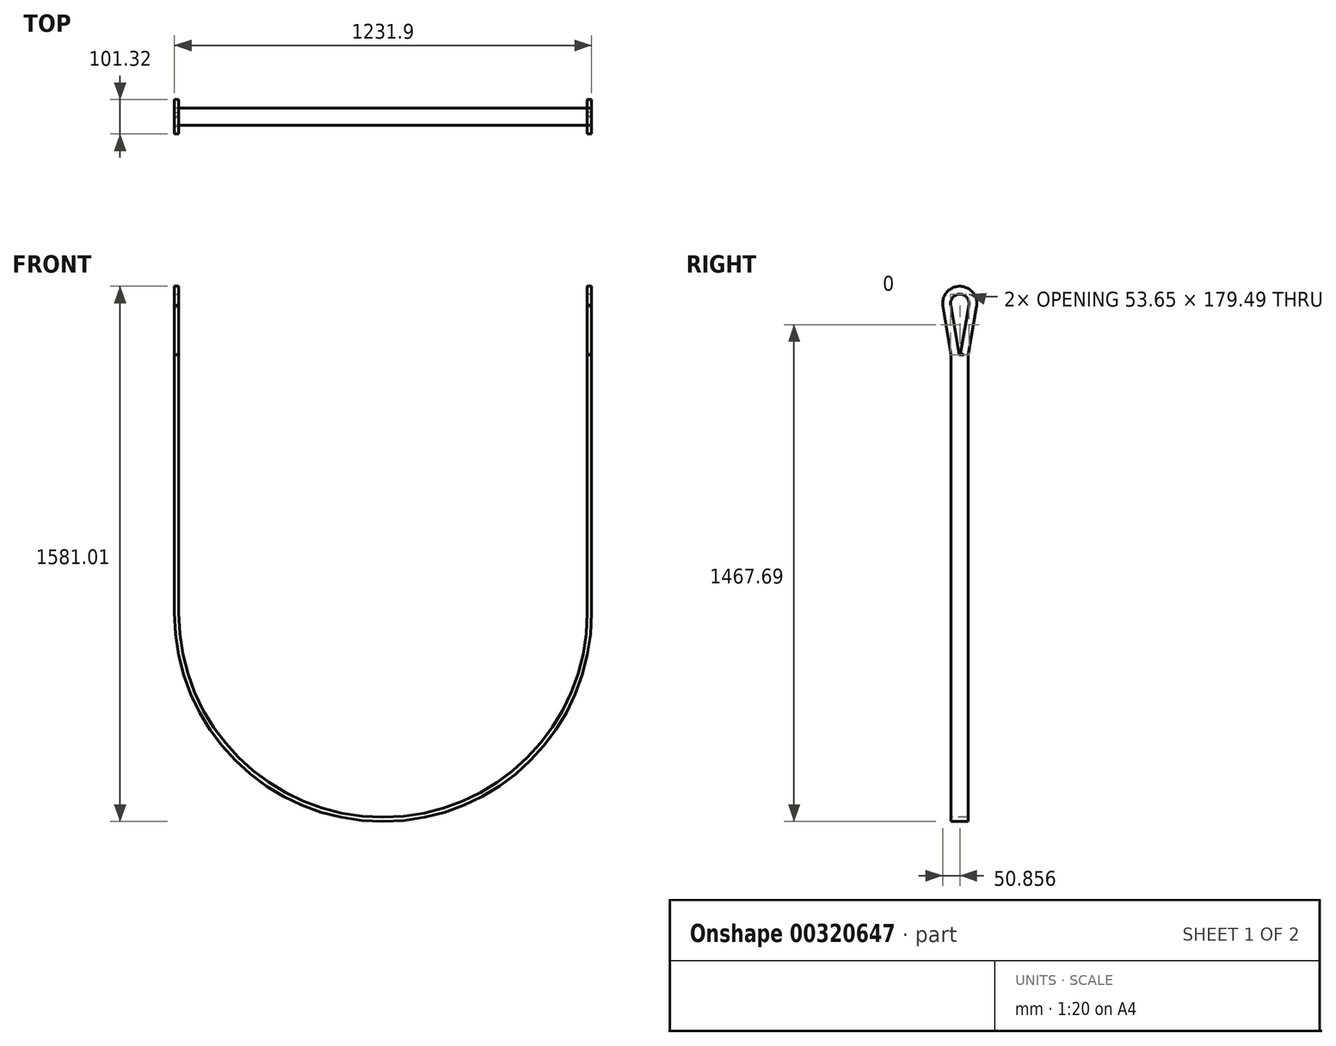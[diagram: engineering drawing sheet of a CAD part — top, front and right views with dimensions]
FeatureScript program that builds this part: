
annotation { "Feature Type Name" : "Feature", "Feature Type Description" : "" }
export const myFeature = defineFeature(function(context is Context, id is Id, definition is map)
    precondition{}
    {
        {
            var Q0;
            Q0=qCreatedBy(makeId("Front.planeOp"),FACE);
            var sketch = newSketch(context, id + "F0", { "sketchPlane" : qUnion([Q0])});
            skLineSegment(sketch, "E0", {"start": v(0, 0) * mm, "end": v(0, -762) * mm, "construction": true});
            skArc(sketch, "E1", {"start": v(-609.6, -762) * mm, "mid": v(0, -1371.6) * mm, "end": v(609.6, -762) * mm});
            skLineSegment(sketch, "E2", {"start": v(-812.59, -762) * mm, "end": v(825.19, -762) * mm, "construction": true});
            skLineSegment(sketch, "E3", {"start": v(-609.6, -762) * mm, "end": v(-609.6, 0) * mm});
            skLineSegment(sketch, "E4.MirrorCS", {"start": v(609.6, -762) * mm, "end": v(609.6, 0) * mm});
            skSolve(sketch);
        }
        {
            var Q0;
            Q0=qCreatedBy(makeId("Top.planeOp"),FACE);
            var sketch = newSketch(context, id + "F1", { "sketchPlane" : qUnion([Q0])});
            skPoint(sketch, "E5.0", {"position": v(-609.6, 0) * mm});
            skLineSegment(sketch, "E6.bottom", {"start": v(-615.95, 25.4) * mm, "end": v(-603.25, 25.4) * mm});
            skLineSegment(sketch, "E6.top", {"start": v(-615.95, -25.4) * mm, "end": v(-603.25, -25.4) * mm});
            skLineSegment(sketch, "E6.left", {"start": v(-615.95, 25.4) * mm, "end": v(-615.95, -25.4) * mm});
            skLineSegment(sketch, "E6.right", {"start": v(-603.25, 25.4) * mm, "end": v(-603.25, -25.4) * mm});
            skSolve(sketch);
        }
        {
            var Q0;
            Q0=makeQuery(id+"F1.imprint","IMPRINT",FACE,{"disambiguationData":[TD([[makeQuery(id+"F1.imprint","IMPRINT",EDGE,{"derivedFrom":sQuery(id+"F1.wireOp",EDGE,"E6.bottom")}),-1.0]])]});
            var Q1;
            Q1=sQuery(id+"F0.wireOp",EDGE,"E3");
            var Q2;
            Q2=sQuery(id+"F0.wireOp",EDGE,"E1");
            var Q3;
            Q3=sQuery(id+"F0.wireOp",EDGE,"E4.MirrorCS");
            sweep(context, id + "F2", {"profiles" : qUnion([Q0]), "path" : qUnion([Q1, Q2, Q3])});
        }
        {
            var Q0;
            Q0=makeQuery(id+"F2.opSweep","SWEPT_FACE",FACE,{"disambiguationData":[OSD([sQuery(id+"F0.wireOp",EDGE,"E4.MirrorCS"),sQuery(id+"F1.wireOp",EDGE,"E6.left")])]});
            var Q1;
            Q1=makeQuery(id+"F2.opSweep","SWEPT_FACE",FACE,{"disambiguationData":[OSD([sQuery(id+"F0.wireOp",EDGE,"E4.MirrorCS"),sQuery(id+"F1.wireOp",EDGE,"E6.right")])]});
            cPlane(context, id + "F3", {"entities" : qUnion([Q0, Q1]), "cplaneType" : CPlaneType.MID_PLANE, "offset" : 25.4 * mm, "width" : 152.4 * mm, "height" : 152.4 * mm});
        }
        {
            var Q0;
            Q0=qCreatedBy(id+"F3.planeOp",FACE);
            var sketch = newSketch(context, id + "F4", { "sketchPlane" : qUnion([Q0])});
            skPoint(sketch, "E7.0", {"position": v(0, 0) * mm});
            skPoint(sketch, "E8.0", {"position": v(-25.4, 0) * mm});
            skLineSegment(sketch, "E9", {"start": v(0, 152.4) * mm, "end": v(0, -21.1) * mm, "construction": true});
            skLineSegment(sketch, "E10.0", {"start": v(-25.4, 0) * mm, "end": v(0, 0) * mm, "construction": true});
            skPoint(sketch, "E11.orphan", {"position": v(25.4, 0) * mm});
            skArc(sketch, "E12", {"start": v(37.56, 146) * mm, "mid": v(0, 190.5) * mm, "end": v(-37.56, 146) * mm});
            skLineSegment(sketch, "E13", {"start": v(-12.7, 0) * mm, "end": v(-37.56, 146) * mm});
            skLineSegment(sketch, "E14.MirrorCS", {"start": v(12.7, 0) * mm, "end": v(37.56, 146) * mm});
            skSolve(sketch);
        }
        {
            var Q0;
            Q0=makeQuery(id+"F2.opSweep","CAP_FACE",FACE,{"disambiguationData":[OSD([sQuery(id+"F0.wireOp",VERTEX,"E4.MirrorCS.end"),sQuery(id+"F1.wireOp",EDGE,"E6.bottom"),sQuery(id+"F1.wireOp",EDGE,"E6.top"),sQuery(id+"F1.wireOp",EDGE,"E6.left"),sQuery(id+"F1.wireOp",EDGE,"E6.right")])],"isStart":false});
            var sketch = newSketch(context, id + "F5", { "sketchPlane" : qUnion([Q0])});
            skLineSegment(sketch, "E15.bottom", {"start": v(615.95, -25.4) * mm, "end": v(603.25, -25.4) * mm});
            skLineSegment(sketch, "E15.top", {"start": v(615.95, -1.53) * mm, "end": v(603.25, -1.53) * mm});
            skLineSegment(sketch, "E15.left", {"start": v(615.95, -25.4) * mm, "end": v(615.95, -1.53) * mm});
            skLineSegment(sketch, "E15.right", {"start": v(603.25, -25.4) * mm, "end": v(603.25, -1.53) * mm});
            skSolve(sketch);
        }
        {
            var Q0;
            Q0=makeQuery(id+"F5.imprint","IMPRINT",FACE,{"disambiguationData":[TD([[makeQuery(id+"F5.imprint","IMPRINT",EDGE,{"derivedFrom":sQuery(id+"F5.wireOp",EDGE,"E15.bottom")}),1.0]])]});
            var Q1;
            Q1=sQuery(id+"F4.wireOp",EDGE,"E13");
            var Q2;
            Q2=sQuery(id+"F4.wireOp",EDGE,"E12");
            var Q3;
            Q3=sQuery(id+"F4.wireOp",EDGE,"E14.MirrorCS");
            sweep(context, id + "F6", {"profiles" : qUnion([Q0]), "path" : qUnion([Q1, Q2, Q3])});
        }
        {
            var Q0;
            Q0=makeQuery(id+"F6.opSweep","SWEPT_BODY",BODY,{"disambiguationData":[OSD([sQuery(id+"F4.wireOp",EDGE,"E14.MirrorCS"),sQuery(id+"F5.wireOp",EDGE,"E15.bottom"),sQuery(id+"F5.wireOp",EDGE,"E15.top"),sQuery(id+"F5.wireOp",EDGE,"E15.left"),sQuery(id+"F5.wireOp",EDGE,"E15.right")])]});
            var Q1;
            Q1=qCreatedBy(makeId("Right.planeOp"),FACE);
            mirror(context, id + "F7", {"operationType" : NewBodyOperationType.ADD, "entities" : qUnion([Q0]), "mirrorPlane" : qUnion([Q1])});
        }
    });
